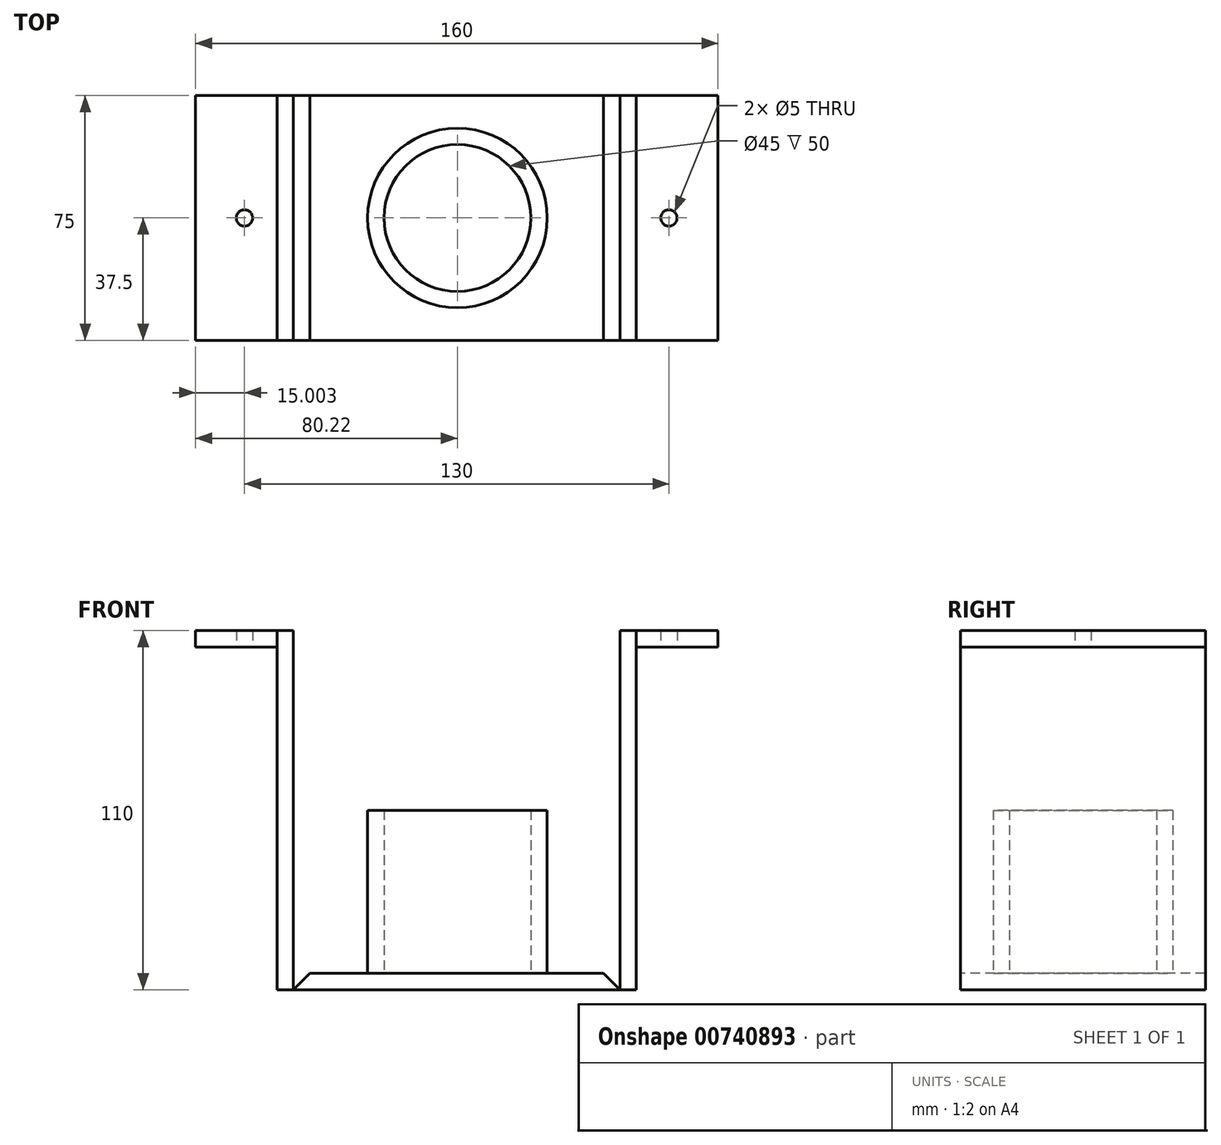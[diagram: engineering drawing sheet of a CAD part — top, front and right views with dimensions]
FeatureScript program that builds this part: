
annotation { "Feature Type Name" : "Feature", "Feature Type Description" : "" }
export const myFeature = defineFeature(function(context is Context, id is Id, definition is map)
    precondition{}
    {
        {
            var Q0;
            Q0=qCreatedBy(makeId("Top.planeOp"),FACE);
            var sketch = newSketch(context, id + "F0", { "sketchPlane" : qUnion([Q0])});
            skLineSegment(sketch, "E0", {"start": v(0, 37.5) * mm, "end": v(0, -37.5) * mm});
            skLineSegment(sketch, "E1", {"start": v(-80.22, 0) * mm, "end": v(79.78, 0) * mm});
            skLineSegment(sketch, "E2.bottom", {"start": v(-80.22, 37.5) * mm, "end": v(-50.22, 37.5) * mm});
            skLineSegment(sketch, "E2.top", {"start": v(-80.22, -37.5) * mm, "end": v(-50.22, -37.5) * mm});
            skLineSegment(sketch, "E2.left", {"start": v(-80.22, 37.5) * mm, "end": v(-80.22, -37.5) * mm});
            skLineSegment(sketch, "E2.right", {"start": v(-50.22, 37.5) * mm, "end": v(-50.22, -37.5) * mm});
            skLineSegment(sketch, "E3.bottom", {"start": v(-50.22, -37.5) * mm, "end": v(49.78, -37.5) * mm});
            skLineSegment(sketch, "E3.top", {"start": v(-50.22, 37.5) * mm, "end": v(49.78, 37.5) * mm});
            skLineSegment(sketch, "E3.left", {"start": v(-50.22, -37.5) * mm, "end": v(-50.22, 37.5) * mm});
            skLineSegment(sketch, "E3.right", {"start": v(49.78, -37.5) * mm, "end": v(49.78, 37.5) * mm});
            skLineSegment(sketch, "E4.bottom", {"start": v(49.78, 37.5) * mm, "end": v(79.78, 37.5) * mm});
            skLineSegment(sketch, "E4.top", {"start": v(49.78, -37.5) * mm, "end": v(79.78, -37.5) * mm});
            skLineSegment(sketch, "E4.left", {"start": v(49.78, 37.5) * mm, "end": v(49.78, -37.5) * mm});
            skLineSegment(sketch, "E4.right", {"start": v(79.78, 37.5) * mm, "end": v(79.78, -37.5) * mm});
            skLineSegment(sketch, "E5", {"start": v(-50.22, 0) * mm, "end": v(-80.22, 0) * mm});
            skLineSegment(sketch, "E6", {"start": v(49.78, 0) * mm, "end": v(79.78, 0) * mm});
            skCircle(sketch, "E7", {"center": v(0, 0) * mm, "radius": 22.5 * mm});
            skCircle(sketch, "E8.0", {"center": v(0, 0) * mm, "radius": 27.5 * mm});
            skCircle(sketch, "E9", {"center": v(-65.22, 0) * mm, "radius": 2.5 * mm});
            skCircle(sketch, "E10", {"center": v(64.78, 0) * mm, "radius": 2.5 * mm});
            skLineSegment(sketch, "E11.bottom", {"start": v(-50.22, 37.5) * mm, "end": v(-55.22, 37.5) * mm});
            skLineSegment(sketch, "E11.top", {"start": v(-50.22, -37.5) * mm, "end": v(-55.22, -37.5) * mm});
            skLineSegment(sketch, "E11.right", {"start": v(-55.22, 37.5) * mm, "end": v(-55.22, -37.5) * mm});
            skLineSegment(sketch, "E12.bottom", {"start": v(49.78, 37.5) * mm, "end": v(54.78, 37.5) * mm});
            skLineSegment(sketch, "E12.top", {"start": v(49.78, -37.5) * mm, "end": v(54.78, -37.5) * mm});
            skLineSegment(sketch, "E12.right", {"start": v(54.78, 37.5) * mm, "end": v(54.78, -37.5) * mm});
            skSolve(sketch);
        }
        {
            var Q0;
            {var subQ0=sQuery(id+"F0.wireOp",EDGE,"E2.right");var subQ1=sQuery(id+"F0.wireOp",EDGE,"E1");var subQ2=makeQuery(id+"F0.imprint","INTERSECT",VERTEX,{"derivedFrom":[subQ1,subQ0]});Q0=makeQuery(id+"F0.imprint","IMPRINT",FACE,{"disambiguationData":[TD([[makeQuery(id+"F0.imprint","IMPRINT",EDGE,{"disambiguationData":[TD([[subQ2,1.0]])],"derivedFrom":subQ1}),1.0]])]});}
            var Q1;
            {var subQ0=sQuery(id+"F0.wireOp",EDGE,"E2.right");var subQ1=sQuery(id+"F0.wireOp",EDGE,"E1");var subQ2=makeQuery(id+"F0.imprint","INTERSECT",VERTEX,{"derivedFrom":[subQ1,subQ0]});Q1=makeQuery(id+"F0.imprint","IMPRINT",FACE,{"disambiguationData":[TD([[makeQuery(id+"F0.imprint","IMPRINT",EDGE,{"disambiguationData":[TD([[subQ2,1.0]])],"derivedFrom":subQ1}),-1.0]])]});}
            var Q2;
            {var subQ0=sQuery(id+"F0.wireOp",EDGE,"E3.right");var subQ1=sQuery(id+"F0.wireOp",EDGE,"E1");var subQ2=makeQuery(id+"F0.imprint","INTERSECT",VERTEX,{"derivedFrom":[subQ1,subQ0]});Q2=makeQuery(id+"F0.imprint","IMPRINT",FACE,{"disambiguationData":[TD([[makeQuery(id+"F0.imprint","IMPRINT",EDGE,{"disambiguationData":[TD([[subQ2,-1.0]])],"derivedFrom":subQ1}),-1.0]])]});}
            var Q3;
            {var subQ0=sQuery(id+"F0.wireOp",EDGE,"E3.right");var subQ1=sQuery(id+"F0.wireOp",EDGE,"E1");var subQ2=makeQuery(id+"F0.imprint","INTERSECT",VERTEX,{"derivedFrom":[subQ1,subQ0]});Q3=makeQuery(id+"F0.imprint","IMPRINT",FACE,{"disambiguationData":[TD([[makeQuery(id+"F0.imprint","IMPRINT",EDGE,{"disambiguationData":[TD([[subQ2,-1.0]])],"derivedFrom":subQ1}),1.0]])]});}
            extrude(context, id + "F1", {"entities" : qUnion([Q0, Q1, Q2, Q3]), "depth" : 110 * mm, "offsetDistance" : 25 * mm});
        }
        {
            var Q0;
            {var subQ0=sQuery(id+"F0.wireOp",EDGE,"E3.top");var subQ3=sQuery(id+"F0.wireOp",EDGE,"E0");var subQ4=makeQuery(id+"F0.imprint","INTERSECT",VERTEX,{"derivedFrom":[subQ3,subQ0]});Q0=makeQuery(id+"F0.imprint","IMPRINT",FACE,{"disambiguationData":[TD([[makeQuery(id+"F0.imprint","IMPRINT",EDGE,{"disambiguationData":[TD([[subQ4,-1.0]])],"derivedFrom":subQ3}),-1.0]])]});}
            var Q1;
            {var subQ3=sQuery(id+"F0.wireOp",EDGE,"E3.bottom");var subQ7=sQuery(id+"F0.wireOp",EDGE,"E0");var subQ8=makeQuery(id+"F0.imprint","INTERSECT",VERTEX,{"derivedFrom":[subQ7,subQ3]});Q1=makeQuery(id+"F0.imprint","IMPRINT",FACE,{"disambiguationData":[TD([[makeQuery(id+"F0.imprint","IMPRINT",EDGE,{"disambiguationData":[TD([[subQ8,1.0]])],"derivedFrom":subQ7}),-1.0]])]});}
            var Q2;
            {var subQ1=sQuery(id+"F0.wireOp",EDGE,"E3.bottom");var subQ3=sQuery(id+"F0.wireOp",EDGE,"E0");var subQ4=makeQuery(id+"F0.imprint","INTERSECT",VERTEX,{"derivedFrom":[subQ3,subQ1]});Q2=makeQuery(id+"F0.imprint","IMPRINT",FACE,{"disambiguationData":[TD([[makeQuery(id+"F0.imprint","IMPRINT",EDGE,{"disambiguationData":[TD([[subQ4,1.0]])],"derivedFrom":subQ3}),1.0]])]});}
            var Q3;
            {var subQ1=sQuery(id+"F0.wireOp",EDGE,"E3.top");var subQ3=sQuery(id+"F0.wireOp",EDGE,"E0");var subQ4=makeQuery(id+"F0.imprint","INTERSECT",VERTEX,{"derivedFrom":[subQ3,subQ1]});Q3=makeQuery(id+"F0.imprint","IMPRINT",FACE,{"disambiguationData":[TD([[makeQuery(id+"F0.imprint","IMPRINT",EDGE,{"disambiguationData":[TD([[subQ4,-1.0]])],"derivedFrom":subQ3}),1.0]])]});}
            var Q4;
            {var subQ0=sQuery(id+"F0.wireOp",EDGE,"E7");var subQ1=sQuery(id+"F0.wireOp",EDGE,"E0");var subQ2=makeQuery(id+"F0.imprint","INTERSECT",VERTEX,{"disambiguationData":[OD(0.0)],"derivedFrom":[subQ1,subQ0]});Q4=makeQuery(id+"F0.imprint","IMPRINT",FACE,{"disambiguationData":[TD([[makeQuery(id+"F0.imprint","IMPRINT",EDGE,{"disambiguationData":[TD([[subQ2,1.0]])],"derivedFrom":subQ1}),1.0]])]});}
            var Q5;
            {var subQ0=sQuery(id+"F0.wireOp",EDGE,"E7");var subQ1=sQuery(id+"F0.wireOp",EDGE,"E0");var subQ2=makeQuery(id+"F0.imprint","INTERSECT",VERTEX,{"disambiguationData":[OD(0.0)],"derivedFrom":[subQ1,subQ0]});Q5=makeQuery(id+"F0.imprint","IMPRINT",FACE,{"disambiguationData":[TD([[makeQuery(id+"F0.imprint","IMPRINT",EDGE,{"disambiguationData":[TD([[subQ2,-1.0]])],"derivedFrom":subQ1}),1.0]])]});}
            var Q6;
            {var subQ0=sQuery(id+"F0.wireOp",EDGE,"E7");var subQ1=sQuery(id+"F0.wireOp",EDGE,"E0");var subQ2=makeQuery(id+"F0.imprint","INTERSECT",VERTEX,{"disambiguationData":[OD(0.0)],"derivedFrom":[subQ1,subQ0]});Q6=makeQuery(id+"F0.imprint","IMPRINT",FACE,{"disambiguationData":[TD([[makeQuery(id+"F0.imprint","IMPRINT",EDGE,{"disambiguationData":[TD([[subQ2,-1.0]])],"derivedFrom":subQ1}),-1.0]])]});}
            var Q7;
            {var subQ0=sQuery(id+"F0.wireOp",EDGE,"E1");var subQ1=sQuery(id+"F0.wireOp",EDGE,"E0");var subQ2=makeQuery(id+"F0.imprint","INTERSECT",VERTEX,{"derivedFrom":[subQ1,subQ0]});Q7=makeQuery(id+"F0.imprint","IMPRINT",FACE,{"disambiguationData":[TD([[makeQuery(id+"F0.imprint","IMPRINT",EDGE,{"disambiguationData":[TD([[subQ2,-1.0]])],"derivedFrom":subQ1}),1.0]])]});}
            var Q8;
            {var subQ0=sQuery(id+"F0.wireOp",EDGE,"E7");var subQ1=sQuery(id+"F0.wireOp",EDGE,"E0");var subQ2=makeQuery(id+"F0.imprint","INTERSECT",VERTEX,{"disambiguationData":[OD(1.0)],"derivedFrom":[subQ1,subQ0]});Q8=makeQuery(id+"F0.imprint","IMPRINT",FACE,{"disambiguationData":[TD([[makeQuery(id+"F0.imprint","IMPRINT",EDGE,{"disambiguationData":[TD([[subQ2,-1.0]])],"derivedFrom":subQ1}),-1.0]])]});}
            var Q9;
            {var subQ0=sQuery(id+"F0.wireOp",EDGE,"E1");var subQ1=sQuery(id+"F0.wireOp",EDGE,"E0");var subQ2=makeQuery(id+"F0.imprint","INTERSECT",VERTEX,{"derivedFrom":[subQ1,subQ0]});Q9=makeQuery(id+"F0.imprint","IMPRINT",FACE,{"disambiguationData":[TD([[makeQuery(id+"F0.imprint","IMPRINT",EDGE,{"disambiguationData":[TD([[subQ2,-1.0]])],"derivedFrom":subQ1}),-1.0]])]});}
            var Q10;
            {var subQ0=sQuery(id+"F0.wireOp",EDGE,"E7");var subQ1=sQuery(id+"F0.wireOp",EDGE,"E0");var subQ2=makeQuery(id+"F0.imprint","INTERSECT",VERTEX,{"disambiguationData":[OD(1.0)],"derivedFrom":[subQ1,subQ0]});Q10=makeQuery(id+"F0.imprint","IMPRINT",FACE,{"disambiguationData":[TD([[makeQuery(id+"F0.imprint","IMPRINT",EDGE,{"disambiguationData":[TD([[subQ2,-1.0]])],"derivedFrom":subQ1}),1.0]])]});}
            var Q11;
            {var subQ0=sQuery(id+"F0.wireOp",EDGE,"E7");var subQ1=sQuery(id+"F0.wireOp",EDGE,"E0");var subQ2=makeQuery(id+"F0.imprint","INTERSECT",VERTEX,{"disambiguationData":[OD(0.0)],"derivedFrom":[subQ1,subQ0]});Q11=makeQuery(id+"F0.imprint","IMPRINT",FACE,{"disambiguationData":[TD([[makeQuery(id+"F0.imprint","IMPRINT",EDGE,{"disambiguationData":[TD([[subQ2,1.0]])],"derivedFrom":subQ1}),-1.0]])]});}
            extrude(context, id + "F2", {"entities" : qUnion([Q0, Q1, Q2, Q3, Q4, Q5, Q6, Q7, Q8, Q9, Q10, Q11]), "depth" : 5 * mm, "offsetDistance" : 25 * mm});
        }
        {
            var Q0;
            {var subQ0=sQuery(id+"F0.wireOp",EDGE,"E7");var subQ1=sQuery(id+"F0.wireOp",EDGE,"E0");var subQ2=makeQuery(id+"F0.imprint","INTERSECT",VERTEX,{"disambiguationData":[OD(1.0)],"derivedFrom":[subQ1,subQ0]});Q0=makeQuery(id+"F0.imprint","IMPRINT",FACE,{"disambiguationData":[TD([[makeQuery(id+"F0.imprint","IMPRINT",EDGE,{"disambiguationData":[TD([[subQ2,-1.0]])],"derivedFrom":subQ1}),1.0]])]});}
            var Q1;
            {var subQ0=sQuery(id+"F0.wireOp",EDGE,"E7");var subQ1=sQuery(id+"F0.wireOp",EDGE,"E0");var subQ2=makeQuery(id+"F0.imprint","INTERSECT",VERTEX,{"disambiguationData":[OD(1.0)],"derivedFrom":[subQ1,subQ0]});Q1=makeQuery(id+"F0.imprint","IMPRINT",FACE,{"disambiguationData":[TD([[makeQuery(id+"F0.imprint","IMPRINT",EDGE,{"disambiguationData":[TD([[subQ2,-1.0]])],"derivedFrom":subQ1}),-1.0]])]});}
            var Q2;
            {var subQ0=sQuery(id+"F0.wireOp",EDGE,"E7");var subQ1=sQuery(id+"F0.wireOp",EDGE,"E0");var subQ2=makeQuery(id+"F0.imprint","INTERSECT",VERTEX,{"disambiguationData":[OD(0.0)],"derivedFrom":[subQ1,subQ0]});Q2=makeQuery(id+"F0.imprint","IMPRINT",FACE,{"disambiguationData":[TD([[makeQuery(id+"F0.imprint","IMPRINT",EDGE,{"disambiguationData":[TD([[subQ2,1.0]])],"derivedFrom":subQ1}),-1.0]])]});}
            var Q3;
            {var subQ0=sQuery(id+"F0.wireOp",EDGE,"E7");var subQ1=sQuery(id+"F0.wireOp",EDGE,"E0");var subQ2=makeQuery(id+"F0.imprint","INTERSECT",VERTEX,{"disambiguationData":[OD(0.0)],"derivedFrom":[subQ1,subQ0]});Q3=makeQuery(id+"F0.imprint","IMPRINT",FACE,{"disambiguationData":[TD([[makeQuery(id+"F0.imprint","IMPRINT",EDGE,{"disambiguationData":[TD([[subQ2,1.0]])],"derivedFrom":subQ1}),1.0]])]});}
            extrude(context, id + "F3", {"entities" : qUnion([Q0, Q1, Q2, Q3]), "operationType" : NewBodyOperationType.ADD, "depth" : 55 * mm, "offsetDistance" : 25 * mm});
        }
        {
            var Q0;
            {var subQ0=sQuery(id+"F0.wireOp",EDGE,"E2.left");var subQ3=sQuery(id+"F0.wireOp",EDGE,"E1");var subQ4=makeQuery(id+"F0.imprint","INTERSECT",VERTEX,{"derivedFrom":[subQ3,subQ0]});Q0=makeQuery(id+"F0.imprint","IMPRINT",FACE,{"disambiguationData":[TD([[makeQuery(id+"F0.imprint","IMPRINT",EDGE,{"disambiguationData":[TD([[subQ4,-1.0]])],"derivedFrom":subQ3}),1.0]])]});}
            var Q1;
            {var subQ0=sQuery(id+"F0.wireOp",EDGE,"E2.left");var subQ3=sQuery(id+"F0.wireOp",EDGE,"E1");var subQ4=makeQuery(id+"F0.imprint","INTERSECT",VERTEX,{"derivedFrom":[subQ3,subQ0]});Q1=makeQuery(id+"F0.imprint","IMPRINT",FACE,{"disambiguationData":[TD([[makeQuery(id+"F0.imprint","IMPRINT",EDGE,{"disambiguationData":[TD([[subQ4,-1.0]])],"derivedFrom":subQ3}),-1.0]])]});}
            var Q2;
            {var subQ3=sQuery(id+"F0.wireOp",EDGE,"E1");var subQ8=sQuery(id+"F0.wireOp",EDGE,"E10");var subQ10=makeQuery(id+"F0.imprint","INTERSECT",VERTEX,{"disambiguationData":[OD(0.0)],"derivedFrom":[subQ3,subQ8]});Q2=makeQuery(id+"F0.imprint","IMPRINT",FACE,{"disambiguationData":[TD([[makeQuery(id+"F0.imprint","IMPRINT",EDGE,{"disambiguationData":[TD([[subQ10,-1.0]])],"derivedFrom":subQ3}),1.0]])]});}
            var Q3;
            {var subQ3=sQuery(id+"F0.wireOp",EDGE,"E1");var subQ8=sQuery(id+"F0.wireOp",EDGE,"E10");var subQ10=makeQuery(id+"F0.imprint","INTERSECT",VERTEX,{"disambiguationData":[OD(0.0)],"derivedFrom":[subQ3,subQ8]});Q3=makeQuery(id+"F0.imprint","IMPRINT",FACE,{"disambiguationData":[TD([[makeQuery(id+"F0.imprint","IMPRINT",EDGE,{"disambiguationData":[TD([[subQ10,-1.0]])],"derivedFrom":subQ3}),-1.0]])]});}
            extrude(context, id + "F4", {"entities" : qUnion([Q0, Q1, Q2, Q3]), "depth" : 5 * mm, "offsetDistance" : 25 * mm});
        }
        {
            var Q0;
            Q0=makeQuery(id+"F4.opExtrude","SWEPT_BODY",BODY,{"disambiguationData":[OSD([sQuery(id+"F0.wireOp",EDGE,"E4.bottom"),sQuery(id+"F0.wireOp",EDGE,"E4.top"),sQuery(id+"F0.wireOp",EDGE,"E4.right"),sQuery(id+"F0.wireOp",EDGE,"E10"),sQuery(id+"F0.wireOp",EDGE,"E12.right")])]});
            var Q1;
            Q1=makeQuery(id+"F4.opExtrude","SWEPT_BODY",BODY,{"disambiguationData":[OSD([sQuery(id+"F0.wireOp",EDGE,"E2.bottom"),sQuery(id+"F0.wireOp",EDGE,"E2.top"),sQuery(id+"F0.wireOp",EDGE,"E2.left"),sQuery(id+"F0.wireOp",EDGE,"E9"),sQuery(id+"F0.wireOp",EDGE,"E11.right")])]});
            transform(context, id + "F5", {"entities" : qUnion([Q0, Q1]), "transformType" : TransformType.TRANSLATION_3D, "dx" : 0 * mm, "dy" : 0 * mm, "dz" : 105 * mm, "makeCopy" : false});
        }
        {
            var Q0;
            Q0=makeQuery(id+"F2.opExtrude","CAP_EDGE",EDGE,{"disambiguationData":[OSD([sQuery(id+"F0.wireOp",EDGE,"E2.right")])],"isStart":false});
            var Q1;
            Q1=makeQuery(id+"F2.opExtrude","CAP_EDGE",EDGE,{"disambiguationData":[OSD([sQuery(id+"F0.wireOp",EDGE,"E3.right")])],"isStart":false});
            chamfer(context, id + "F6", {"entities" : qUnion([Q0, Q1]), "width" : 5 * mm, "tangentPropagation" : true});
        }
    });
